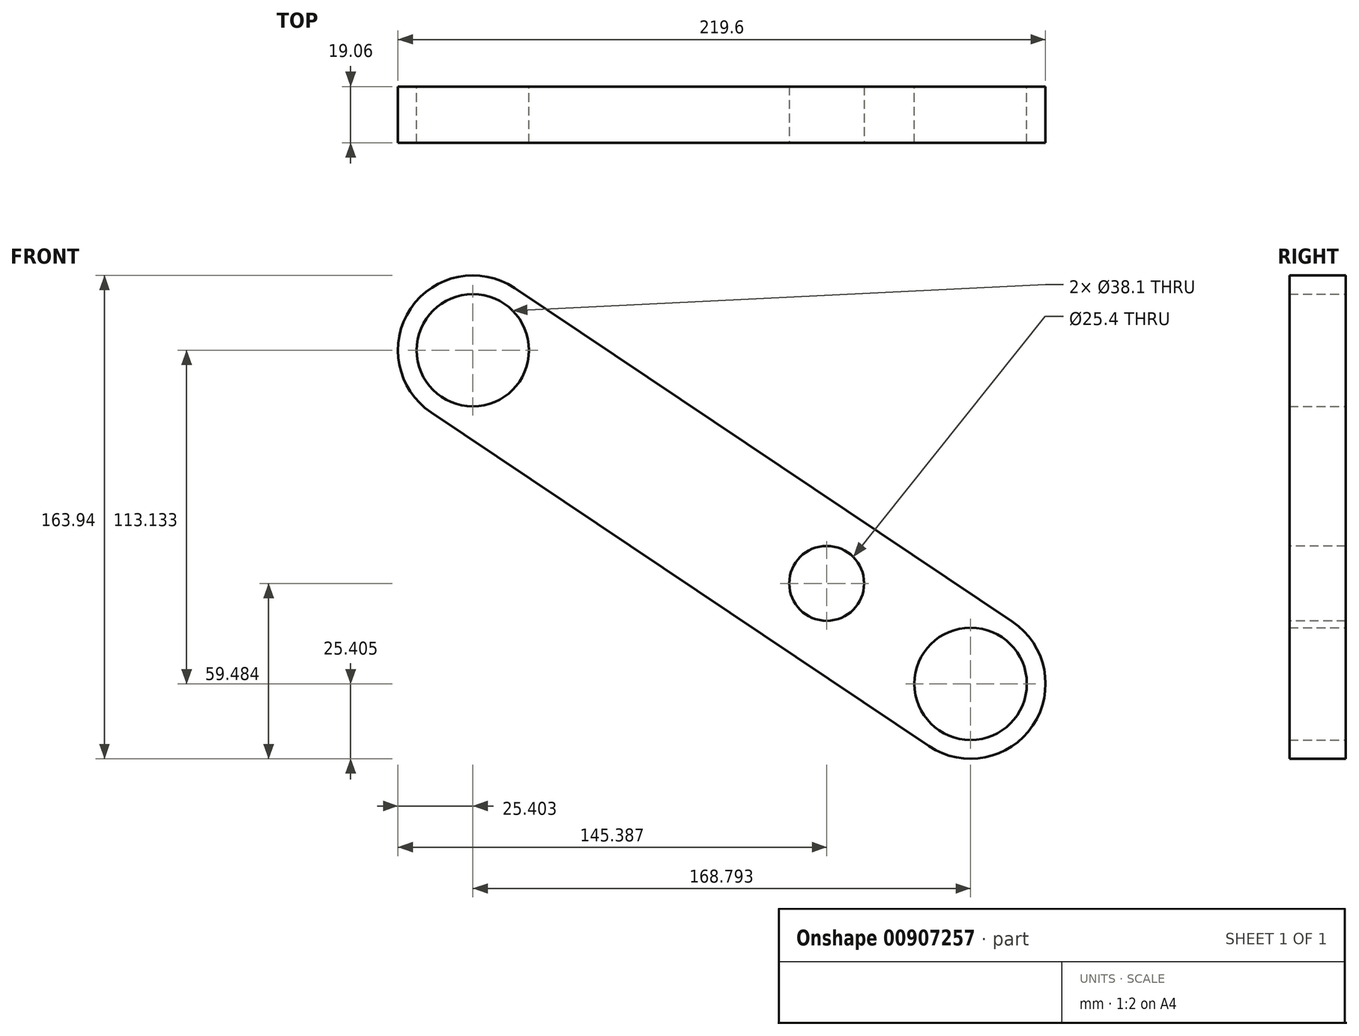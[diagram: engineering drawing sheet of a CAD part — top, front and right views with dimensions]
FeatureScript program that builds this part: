
annotation { "Feature Type Name" : "Feature", "Feature Type Description" : "" }
export const myFeature = defineFeature(function(context is Context, id is Id, definition is map)
    precondition{}
    {
        {
            var Q0;
            Q0=qCreatedBy(makeId("Front.planeOp"),FACE);
            var sketch = newSketch(context, id + "F0", { "sketchPlane" : qUnion([Q0])});
            skLineSegment(sketch, "E0", {"start": v(-72.1, 84.22) * mm, "end": v(96.69, -28.92) * mm});
            skLineSegment(sketch, "E1", {"start": v(-100.39, 42.02) * mm, "end": v(68.4, -71.11) * mm});
            skArc(sketch, "E2", {"start": v(-72.1, 84.22) * mm, "mid": v(-107.35, 77.26) * mm, "end": v(-100.39, 42.02) * mm});
            skArc(sketch, "E3", {"start": v(96.69, -28.92) * mm, "mid": v(103.65, -64.16) * mm, "end": v(68.4, -71.11) * mm});
            skCircle(sketch, "E4", {"center": v(-86.25, 63.12) * mm, "radius": 19.05 * mm});
            skCircle(sketch, "E5", {"center": v(82.55, -50.02) * mm, "radius": 19.05 * mm});
            skSolve(sketch);
        }
        {
            var Q0;
            Q0=qSketchRegion(id+"F0",true);
            extrude(context, id + "F1", {"entities" : qUnion([Q0]), "endBound" : BoundingType.SYMMETRIC, "depth" : 19.05 * mm, "offsetDistance" : 25.4 * mm});
        }
        {
            var Q0;
            Q0=makeQuery(id+"F1.opExtrude","CAP_FACE",FACE,{"disambiguationData":[OSD([sQuery(id+"F0.wireOp",EDGE,"E0"),sQuery(id+"F0.wireOp",EDGE,"E1"),sQuery(id+"F0.wireOp",EDGE,"E2"),sQuery(id+"F0.wireOp",EDGE,"E3"),sQuery(id+"F0.wireOp",EDGE,"E4"),sQuery(id+"F0.wireOp",EDGE,"E5")])],"isStart":false});
            var sketch = newSketch(context, id + "F2", { "sketchPlane" : qUnion([Q0])});
            skCircle(sketch, "E6", {"center": v(33.74, -15.94) * mm, "radius": 12.7 * mm});
            skSolve(sketch);
        }
        {
            var Q0;
            Q0=makeQuery(id+"F2.imprint","IMPRINT",FACE,{"disambiguationData":[TD([[makeQuery(id+"F2.imprint","IMPRINT",EDGE,{"derivedFrom":sQuery(id+"F2.wireOp",EDGE,"E6")}),1.0]])]});
            extrude(context, id + "F3", {"entities" : qUnion([Q0]), "operationType" : NewBodyOperationType.REMOVE, "endBound" : BoundingType.SYMMETRIC, "oppositeDirection" : true, "depth" : 76.2 * mm, "offsetDistance" : 25.4 * mm});
        }
    });
